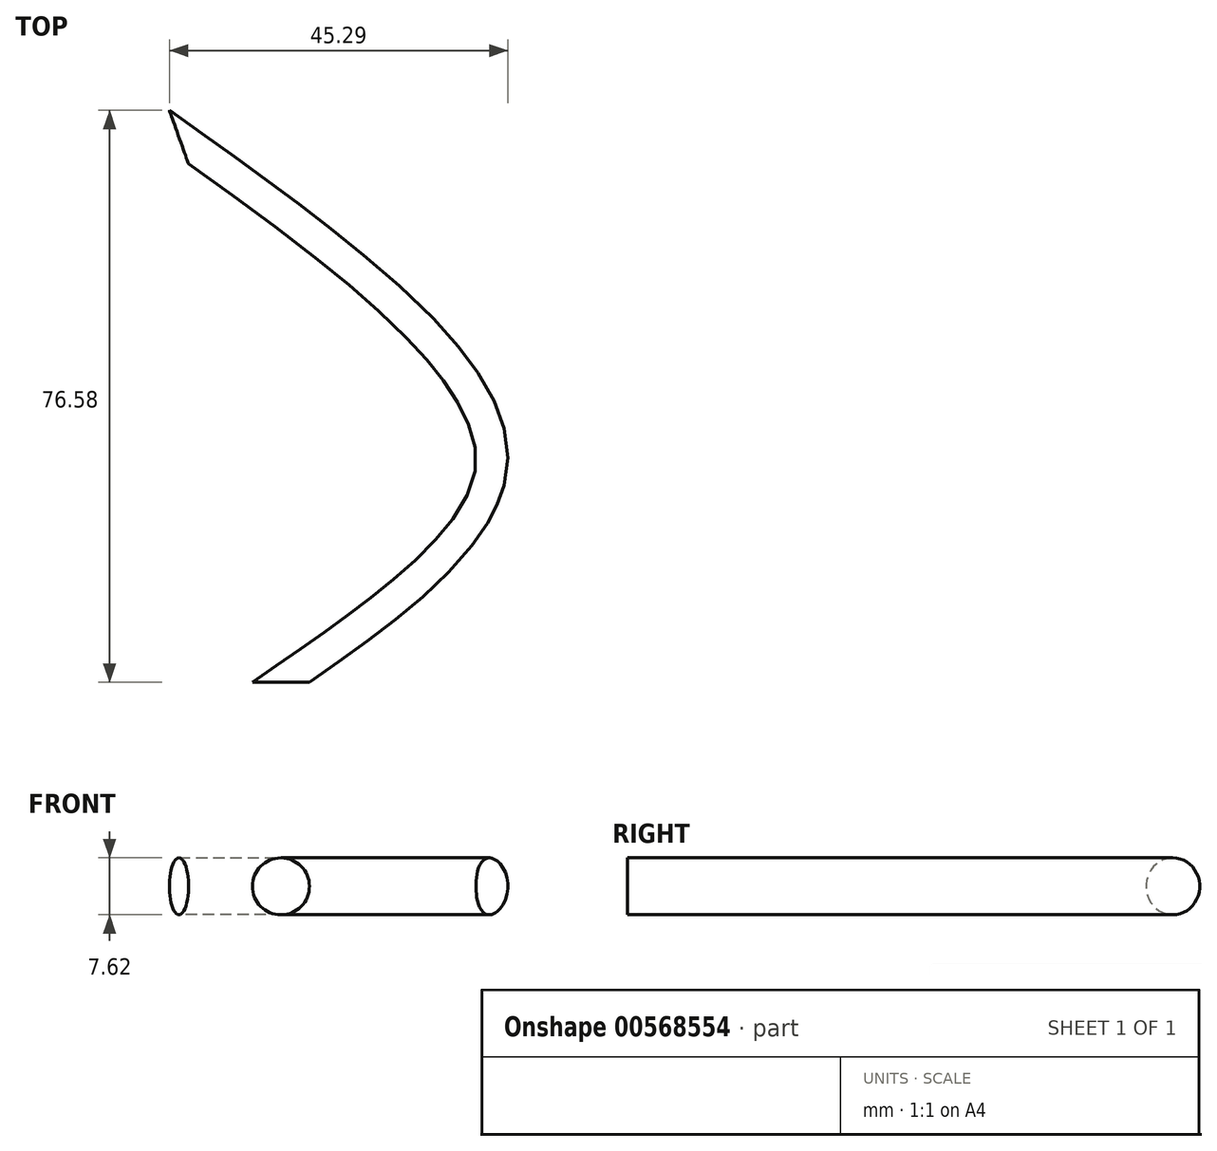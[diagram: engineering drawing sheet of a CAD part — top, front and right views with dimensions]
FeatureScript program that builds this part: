
annotation { "Feature Type Name" : "Feature", "Feature Type Description" : "" }
export const myFeature = defineFeature(function(context is Context, id is Id, definition is map)
    precondition{}
    {
        {
            var Q0;
            Q0=qCreatedBy(makeId("Front.planeOp"),FACE);
            var sketch = newSketch(context, id + "F0", { "sketchPlane" : qUnion([Q0])});
            skCircle(sketch, "E0", {"center": v(0, 0) * mm, "radius": 3.81 * mm});
            skSolve(sketch);
        }
        {
            var Q0;
            Q0=qCreatedBy(makeId("Top.planeOp"),FACE);
            var sketch = newSketch(context, id + "F1", { "sketchPlane" : qUnion([Q0])});
            skFitSpline(sketch, "E1", {"points": [v(0, 0) * mm, v(27.87, 30.34) * mm, v(-13.65, 73) * mm], "startDerivative": vector(92.58, 64.23) * mm, "endDerivative": vector(-113.58, 81.24) * mm});
            skSolve(sketch);
        }
        {
            var Q0;
            Q0=makeQuery(id+"F0.imprint","IMPRINT",FACE,{"disambiguationData":[TD([[makeQuery(id+"F0.imprint","IMPRINT",EDGE,{"derivedFrom":sQuery(id+"F0.wireOp",EDGE,"E0")}),1.0]])]});
            var Q1;
            Q1=sQuery(id+"F1.wireOp",EDGE,"E1");
            sweep(context, id + "F2", {"profiles" : qUnion([Q0]), "path" : qUnion([Q1])});
        }
    });
